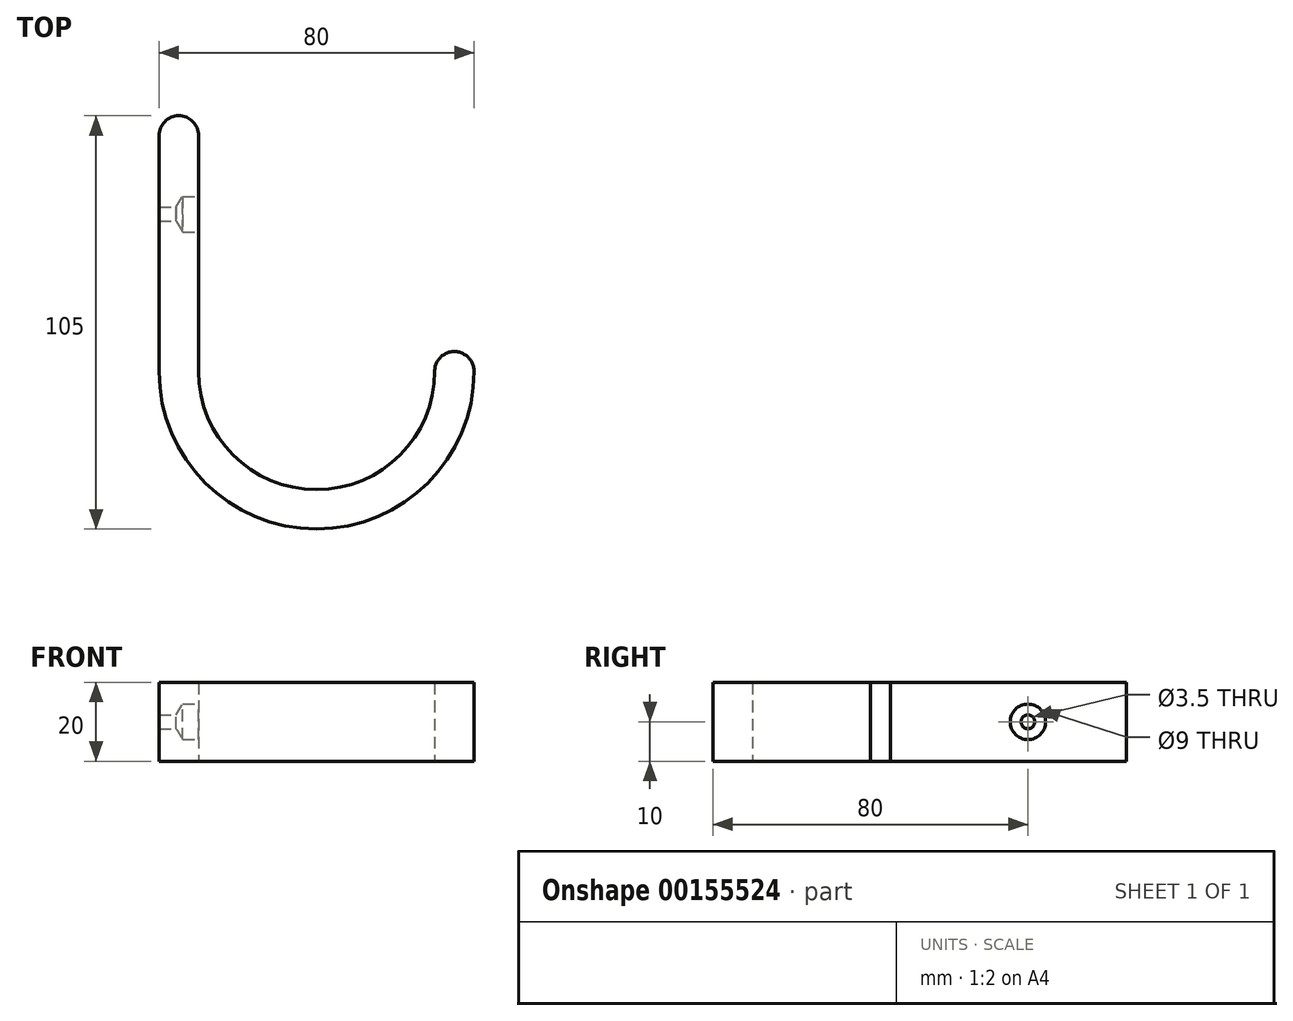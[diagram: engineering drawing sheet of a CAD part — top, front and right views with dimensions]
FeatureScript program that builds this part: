
annotation { "Feature Type Name" : "Feature", "Feature Type Description" : "" }
export const myFeature = defineFeature(function(context is Context, id is Id, definition is map)
    precondition{}
    {
        {
            assignVariable(context, id + "F0", {"name" : "wallWidth", "anyValue" : 10});
        }
        {
            assignVariable(context, id + "F1", {"name" : "screwHoleDiameter", "anyValue" : 3.5});
        }
        {
            assignVariable(context, id + "F2", {"name" : "screwHead", "anyValue" : 9});
        }
        {
            assignVariable(context, id + "F3", {"name" : "hookWidth", "anyValue" : 20});
        }
        {
            assignVariable(context, id + "F4", {"name" : "counterSinkDepth", "anyValue" : 4});
        }
        {
            var Q0;
            Q0=qCreatedBy(makeId("Top.planeOp"),FACE);
            var sketch = newSketch(context, id + "F5", { "sketchPlane" : qUnion([Q0])});
            skArc(sketch, "E0", {"start": v(-30, 0) * mm, "mid": v(0, -30) * mm, "end": v(30, 0) * mm});
            skArc(sketch, "E1", {"start": v(-40, 0) * mm, "mid": v(0, -40) * mm, "end": v(40, 0) * mm});
            skArc(sketch, "E2", {"start": v(40, 0) * mm, "mid": v(35, 5.07) * mm, "end": v(30, 0) * mm});
            skLineSegment(sketch, "E3", {"start": v(-30, 0) * mm, "end": v(-30, 60) * mm});
            skLineSegment(sketch, "E4", {"start": v(-40, 0) * mm, "end": v(-40, 60) * mm});
            skArc(sketch, "E5", {"start": v(-30, 60) * mm, "mid": v(-35, 65) * mm, "end": v(-40, 60) * mm});
            skSolve(sketch);
        }
        {
            var Q0;
            Q0=makeQuery(id+"F5.imprint","IMPRINT",FACE,{"disambiguationData":[TD([[makeQuery(id+"F5.imprint","IMPRINT",EDGE,{"derivedFrom":sQuery(id+"F5.wireOp",EDGE,"E0")}),-1.0]])]});
            extrude(context, id + "F6", {"entities" : qUnion([Q0]), "depth" : (getVariable(context, 'hookWidth')) * mm});
        }
        {
            var Q0;
            Q0=makeQuery(id+"F6.opExtrude","SWEPT_FACE",FACE,{"disambiguationData":[OSD([sQuery(id+"F5.wireOp",EDGE,"E3")])]});
            var sketch = newSketch(context, id + "F7", { "sketchPlane" : qUnion([Q0])});
            skPoint(sketch, "E6", {"position": v(40, 10) * mm});
            skSolve(sketch);
        }
        {
            var Q0;
            Q0=sQuery(id+"F7.wireOp",VERTEX,"E6");
            var Q1;
            Q1=makeQuery(id+"F6.opExtrude","SWEPT_BODY",BODY,{"disambiguationData":[OSD([sQuery(id+"F5.wireOp",EDGE,"E0"),sQuery(id+"F5.wireOp",EDGE,"E1"),sQuery(id+"F5.wireOp",EDGE,"E2"),sQuery(id+"F5.wireOp",EDGE,"E3"),sQuery(id+"F5.wireOp",EDGE,"E4"),sQuery(id+"F5.wireOp",EDGE,"E5")])]});
            hole(context, id + "F8", {"style" : HoleStyle.SIMPLE, "endStyle" : HoleEndStyle.BLIND, "holeDiameter" : (getVariable(context, 'screwHoleDiameter')) * mm, "holeDepth" : (getVariable(context, 'wallWidth')) * mm, "startFromSketch" : true, "locations" : qUnion([Q0]), "scope" : qUnion([Q1])});
        }
        {
            var Q0;
            Q0=sQuery(id+"F7.wireOp",VERTEX,"E6");
            var Q1;
            Q1=makeQuery(id+"F6.opExtrude","SWEPT_BODY",BODY,{"disambiguationData":[OSD([sQuery(id+"F5.wireOp",EDGE,"E0"),sQuery(id+"F5.wireOp",EDGE,"E1"),sQuery(id+"F5.wireOp",EDGE,"E2"),sQuery(id+"F5.wireOp",EDGE,"E3"),sQuery(id+"F5.wireOp",EDGE,"E4"),sQuery(id+"F5.wireOp",EDGE,"E5")])]});
            hole(context, id + "F9", {"style" : HoleStyle.SIMPLE, "endStyle" : HoleEndStyle.BLIND, "holeDiameter" : (getVariable(context, 'screwHead')) * mm, "holeDepth" : (getVariable(context, 'counterSinkDepth')) * mm, "startFromSketch" : true, "locations" : qUnion([Q0]), "scope" : qUnion([Q1])});
        }
    });
